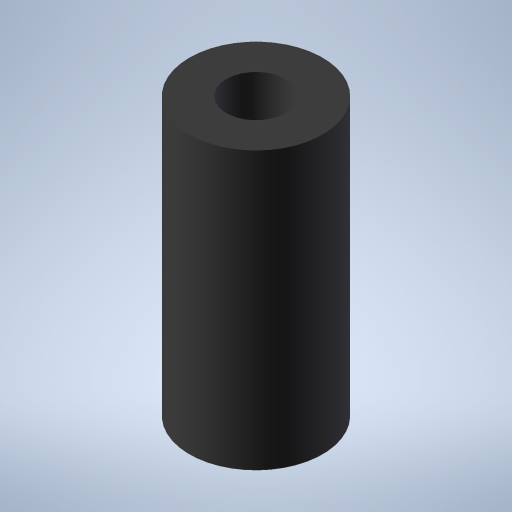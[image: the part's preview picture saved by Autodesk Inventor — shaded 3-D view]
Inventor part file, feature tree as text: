
AUTODESK INVENTOR PART (.ipt)
format: ipt  version: 2023 (Build 270158000, 158)  size: 360,448 bytes
history: native  units: in
note: dims shown in document units (in); Inventor stores cm internally (conversion verified against a paired STEP export)
features: extrude x2, sketch x2
ambient origin geometry x8: Origin, YZ Plane, XZ Plane, XY Plane, X Axis, Y Axis, Z Axis, Center Point
bodies: Solid1 (feature_tree)
feature tree (4):
  extrude  "Extrusion1"  Depth=0.065in
  extrude  "Extrusion2"  Depth=0.2441in
  sketch  "Sketch1"  dims[d0=0.189in d1=0.065in]
  sketch  "Sketch2"  dims[d2=0.3937in d3=0.0in d4=0.0846in d5=0.2441in d6=0.0in]
